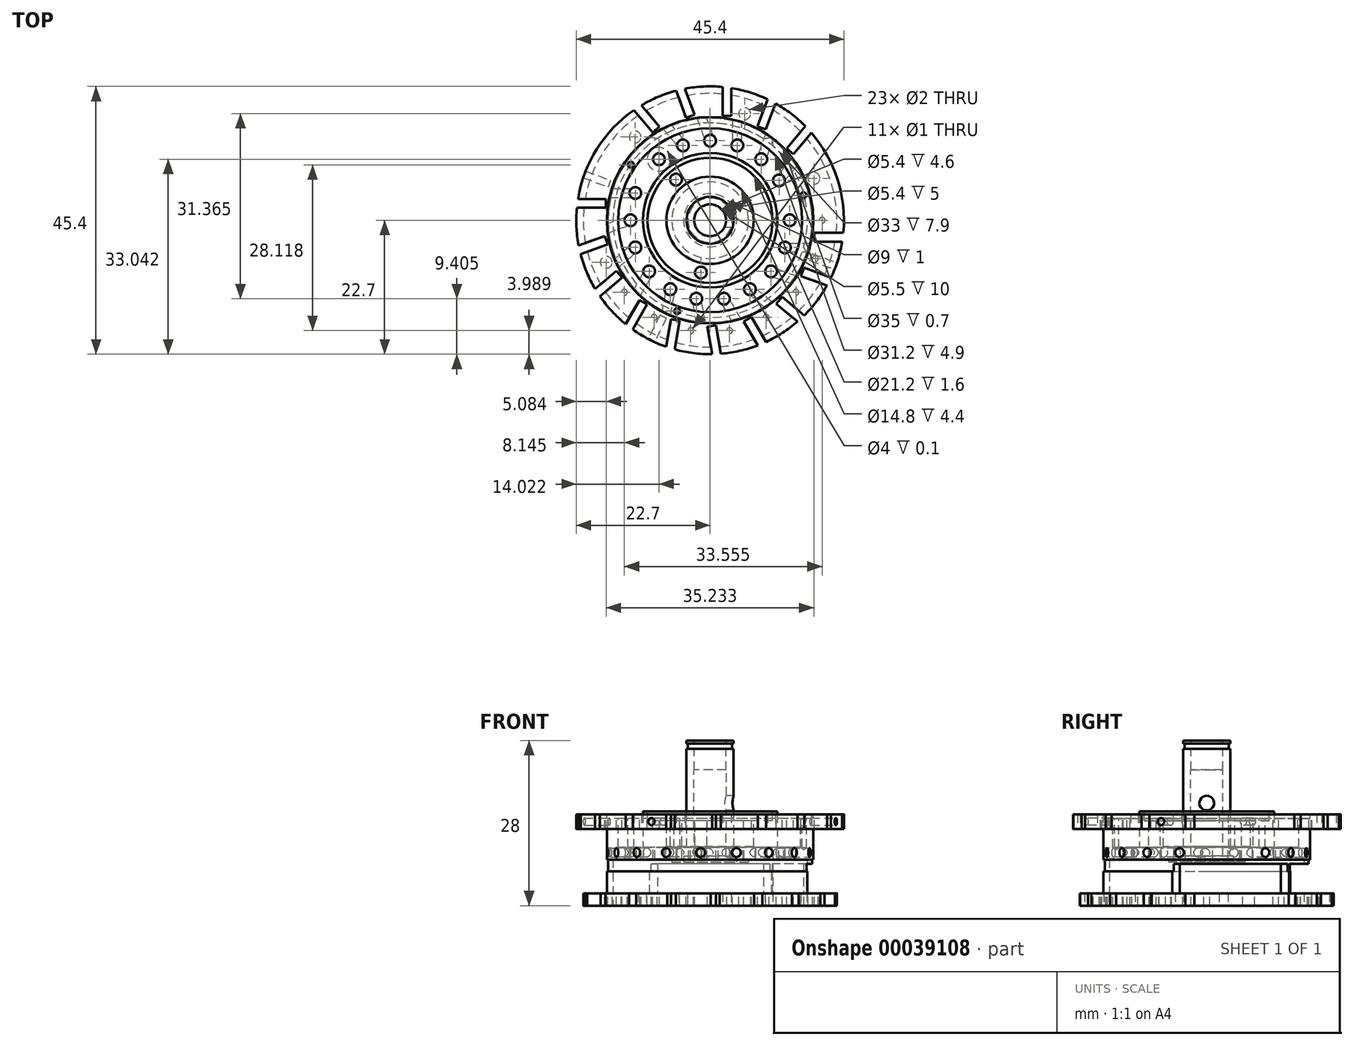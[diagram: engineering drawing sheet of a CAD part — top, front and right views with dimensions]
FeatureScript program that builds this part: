
annotation { "Feature Type Name" : "Feature", "Feature Type Description" : "" }
export const myFeature = defineFeature(function(context is Context, id is Id, definition is map)
    precondition{}
    {
        {
            var Q0;
            Q0=qCreatedBy(makeId("Front.planeOp"),FACE);
            var sketch = newSketch(context, id + "F0", { "sketchPlane" : qUnion([Q0])});
            skLineSegment(sketch, "E0", {"start": v(0, 12.5) * mm, "end": v(4, 12.5) * mm});
            skLineSegment(sketch, "E1", {"start": v(4, 12.5) * mm, "end": v(4, 12) * mm});
            skLineSegment(sketch, "E2", {"start": v(4, 12) * mm, "end": v(3.75, 12) * mm});
            skLineSegment(sketch, "E3", {"start": v(3.75, 12) * mm, "end": v(3.75, 11.1) * mm});
            skLineSegment(sketch, "E4", {"start": v(3.75, 11.1) * mm, "end": v(4, 11.1) * mm});
            skLineSegment(sketch, "E5", {"start": v(4, 11.1) * mm, "end": v(4, 0.5) * mm});
            skLineSegment(sketch, "E6", {"start": v(4, 0.5) * mm, "end": v(11.4, 0.5) * mm});
            skLineSegment(sketch, "E7", {"start": v(11.4, 0.5) * mm, "end": v(11.4, 0) * mm});
            skLineSegment(sketch, "E8", {"start": v(11.4, 0) * mm, "end": v(22.7, 0) * mm});
            skLineSegment(sketch, "E9", {"start": v(22.7, 0) * mm, "end": v(22.7, -2.5) * mm});
            skLineSegment(sketch, "E10", {"start": v(22.7, -2.5) * mm, "end": v(17.5, -2.5) * mm});
            skLineSegment(sketch, "E11", {"start": v(17.5, -2.5) * mm, "end": v(17.5, -7.7) * mm});
            skLineSegment(sketch, "E12", {"start": v(17.5, -7.7) * mm, "end": v(17.3, -7.7) * mm});
            skLineSegment(sketch, "E13", {"start": v(17.3, -7.7) * mm, "end": v(17.3, -9.7) * mm});
            skLineSegment(sketch, "E14", {"start": v(17.3, -9.7) * mm, "end": v(17.5, -9.7) * mm});
            skLineSegment(sketch, "E15", {"start": v(17.5, -9.7) * mm, "end": v(17.5, -13.4) * mm});
            skLineSegment(sketch, "E16", {"start": v(17.5, -13.4) * mm, "end": v(22.7, -13.4) * mm});
            skLineSegment(sketch, "E17", {"start": v(22.7, -13.4) * mm, "end": v(22.7, -15.5) * mm});
            skLineSegment(sketch, "E18", {"start": v(22.7, -15.5) * mm, "end": v(0, -15.5) * mm});
            skLineSegment(sketch, "E19", {"start": v(0, -15.5) * mm, "end": v(0, 12.5) * mm});
            skSolve(sketch);
        }
        {
            var Q0;
            Q0 = qSketchRegion(id + "F0", true);
            var Q1;
            Q1=sQuery(id+"F0.wireOp",EDGE,"E19");
            revolve(context, id + "F1", {"entities" : qUnion([Q0]), "axis" : qUnion([Q1]), "revolveType" : RevolveType.FULL});
        }
        {
            var Q0;
            Q0=qCreatedBy(makeId("Right.planeOp"),FACE);
            var sketch = newSketch(context, id + "F2", { "sketchPlane" : qUnion([Q0])});
            skCircle(sketch, "E20", {"center": v(0, 1.9) * mm, "radius": 1.25 * mm});
            skSolve(sketch);
        }
        {
            var Q0;
            Q0=makeQuery(id+"F2.imprint","IMPRINT",FACE,{"disambiguationData":[TD([[makeQuery(id+"F2.imprint","IMPRINT",EDGE,{"derivedFrom":sQuery(id+"F2.wireOp",EDGE,"E20")}),1.0]])]});
            extrude(context, id + "F3", {"entities" : qUnion([Q0]), "operationType" : NewBodyOperationType.REMOVE, "depth" : 5 * mm});
        }
        {
            var Q0;
            Q0=makeQuery(id+"F1.opRevolve","SWEPT_FACE",FACE,{"disambiguationData":[OSD([sQuery(id+"F0.wireOp",EDGE,"E0")])]});
            var sketch = newSketch(context, id + "F4", { "sketchPlane" : qUnion([Q0])});
            skCircle(sketch, "E21", {"center": v(0, 0) * mm, "radius": 2.7 * mm});
            skSolve(sketch);
        }
        {
            var Q0;
            Q0=makeQuery(id+"F4.imprint","IMPRINT",FACE,{"disambiguationData":[TD([[makeQuery(id+"F4.imprint","IMPRINT",EDGE,{"derivedFrom":sQuery(id+"F4.wireOp",EDGE,"E21")}),1.0]])]});
            var Q1;
            Q1=makeQuery(id+"F1.opRevolve","SWEPT_FACE",FACE,{"disambiguationData":[OSD([sQuery(id+"F0.wireOp",EDGE,"E18")])]});
            extrude(context, id + "F5", {"entities" : qUnion([Q0]), "operationType" : NewBodyOperationType.REMOVE, "endBound" : BoundingType.UP_TO_SURFACE, "oppositeDirection" : true, "endBoundEntityFace" : qUnion([Q1]), "depth" : 5 * mm});
        }
        {
            var Q0;
            Q0=makeQuery(id+"F1.opRevolve","SWEPT_FACE",FACE,{"disambiguationData":[OSD([sQuery(id+"F0.wireOp",EDGE,"E18")])]});
            var sketch = newSketch(context, id + "F6", { "sketchPlane" : qUnion([Q0])});
            skCircle(sketch, "E22", {"center": v(0, 0) * mm, "radius": 16.5 * mm});
            skSolve(sketch);
        }
        {
            var Q0;
            Q0=makeQuery(id+"F6.imprint","IMPRINT",FACE,{"disambiguationData":[TD([[makeQuery(id+"F6.imprint","IMPRINT",EDGE,{"derivedFrom":sQuery(id+"F6.wireOp",EDGE,"E22")}),1.0]])]});
            extrude(context, id + "F7", {"entities" : qUnion([Q0]), "operationType" : NewBodyOperationType.REMOVE, "oppositeDirection" : true, "depth" : 7.4 * mm});
        }
        {
            var Q0;
            Q0=makeQuery(id+"F7.boolean.opBoolean","COPY",FACE,{"derivedFrom":makeQuery(id+"F7.opExtrude","CAP_FACE",FACE,{"disambiguationData":[OSD([sQuery(id+"F6.wireOp",EDGE,"E22")])],"isStart":false})});
            var sketch = newSketch(context, id + "F8", { "sketchPlane" : qUnion([Q0])});
            skCircle(sketch, "E23", {"center": v(0, 0) * mm, "radius": 6.5 * mm});
            skCircle(sketch, "E24", {"center": v(0, 0) * mm, "radius": 16.5 * mm});
            skSolve(sketch);
        }
        {
            var Q0;
            Q0=makeQuery(id+"F8.imprint","IMPRINT",FACE,{"disambiguationData":[TD([[makeQuery(id+"F8.imprint","IMPRINT",EDGE,{"derivedFrom":sQuery(id+"F8.wireOp",EDGE,"E23")}),-1.0]])]});
            extrude(context, id + "F9", {"entities" : qUnion([Q0]), "operationType" : NewBodyOperationType.REMOVE, "oppositeDirection" : true, "depth" : 0.5 * mm});
        }
        {
            var Q0;
            Q0=makeQuery(id+"F7.boolean.opBoolean","COPY",FACE,{"derivedFrom":makeQuery(id+"F7.opExtrude","CAP_FACE",FACE,{"disambiguationData":[OSD([sQuery(id+"F6.wireOp",EDGE,"E22")])],"isStart":false})});
            var sketch = newSketch(context, id + "F10", { "sketchPlane" : qUnion([Q0])});
            skCircle(sketch, "E25", {"center": v(0, 0) * mm, "radius": 4.5 * mm});
            skSolve(sketch);
        }
        {
            var Q0;
            Q0=makeQuery(id+"F10.imprint","IMPRINT",FACE,{"disambiguationData":[TD([[makeQuery(id+"F10.imprint","IMPRINT",EDGE,{"derivedFrom":sQuery(id+"F10.wireOp",EDGE,"E25")}),1.0]])]});
            extrude(context, id + "F11", {"entities" : qUnion([Q0]), "operationType" : NewBodyOperationType.REMOVE, "oppositeDirection" : true, "depth" : 1 * mm});
        }
        {
            var Q0;
            Q0=qCreatedBy(makeId("Top.planeOp"),FACE);
            var sketch = newSketch(context, id + "F12", { "sketchPlane" : qUnion([Q0])});
            skCircle(sketch, "E26", {"center": v(0, 0) * mm, "radius": 2.75 * mm});
            skSolve(sketch);
        }
        {
            var Q0;
            Q0 = qSketchRegion(id + "F12", true);
            extrude(context, id + "F13", {"entities" : qUnion([Q0]), "operationType" : NewBodyOperationType.REMOVE, "oppositeDirection" : true, "depth" : 2.5 * mm, "hasSecondDirection" : true, "secondDirectionOppositeDirection" : false, "secondDirectionDepth" : 7.5 * mm});
        }
        {
            var Q0;
            Q0=makeQuery(id+"F1.opRevolve","SWEPT_FACE",FACE,{"disambiguationData":[OSD([sQuery(id+"F0.wireOp",EDGE,"E8")])]});
            var sketch = newSketch(context, id + "F14", { "sketchPlane" : qUnion([Q0])});
            skCircle(sketch, "E27", {"center": v(0, 0) * mm, "radius": 11.4 * mm});
            skCircle(sketch, "E28", {"center": v(0, 0) * mm, "radius": 15.6 * mm});
            skCircle(sketch, "E29", {"center": v(0, 0) * mm, "radius": 17.5 * mm});
            skSolve(sketch);
        }
        {
            var Q0;
            Q0=makeQuery(id+"F14.imprint","IMPRINT",FACE,{"disambiguationData":[TD([[makeQuery(id+"F14.imprint","IMPRINT",EDGE,{"derivedFrom":sQuery(id+"F14.wireOp",EDGE,"E27")}),1.0]])]});
            var Q1;
            Q1=makeQuery(id+"F14.imprint","IMPRINT",FACE,{"disambiguationData":[TD([[makeQuery(id+"F14.imprint","IMPRINT",EDGE,{"derivedFrom":sQuery(id+"F14.wireOp",EDGE,"E28")}),-1.0]])]});
            extrude(context, id + "F15", {"entities" : qUnion([Q0, Q1]), "operationType" : NewBodyOperationType.REMOVE, "oppositeDirection" : true, "depth" : 0.7 * mm});
        }
        {
            var Q0;
            Q0=makeQuery(id+"F14.imprint","IMPRINT",FACE,{"disambiguationData":[TD([[makeQuery(id+"F14.imprint","IMPRINT",EDGE,{"derivedFrom":sQuery(id+"F14.wireOp",EDGE,"E27")}),1.0]])]});
            extrude(context, id + "F16", {"entities" : qUnion([Q0]), "operationType" : NewBodyOperationType.REMOVE, "oppositeDirection" : true, "depth" : 5.6 * mm});
        }
        {
            var Q0;
            Q0=makeQuery(id+"F1.opRevolve","SWEPT_FACE",FACE,{"disambiguationData":[OSD([sQuery(id+"F0.wireOp",EDGE,"E6")])]});
            var sketch = newSketch(context, id + "F17", { "sketchPlane" : qUnion([Q0])});
            skCircle(sketch, "E30", {"center": v(0, 0) * mm, "radius": 7.4 * mm});
            skCircle(sketch, "E31", {"center": v(0, 0) * mm, "radius": 10.6 * mm});
            skSolve(sketch);
        }
        {
            var Q0;
            Q0=makeQuery(id+"F17.imprint","IMPRINT",FACE,{"disambiguationData":[TD([[makeQuery(id+"F17.imprint","IMPRINT",EDGE,{"derivedFrom":sQuery(id+"F17.wireOp",EDGE,"E30")}),1.0]])]});
            var Q1;
            Q1=makeQuery(id+"F17.imprint","IMPRINT",FACE,{"disambiguationData":[TD([[makeQuery(id+"F17.imprint","IMPRINT",EDGE,{"derivedFrom":sQuery(id+"F17.wireOp",EDGE,"E30")}),-1.0]])]});
            extrude(context, id + "F18", {"entities" : qUnion([Q0, Q1]), "operationType" : NewBodyOperationType.REMOVE, "oppositeDirection" : true, "depth" : 1.6 * mm});
        }
        {
            var Q0;
            Q0=makeQuery(id+"F17.imprint","IMPRINT",FACE,{"disambiguationData":[TD([[makeQuery(id+"F17.imprint","IMPRINT",EDGE,{"derivedFrom":sQuery(id+"F17.wireOp",EDGE,"E30")}),1.0]])]});
            extrude(context, id + "F19", {"entities" : qUnion([Q0]), "operationType" : NewBodyOperationType.REMOVE, "oppositeDirection" : true, "depth" : 6 * mm});
        }
        {
            var Q0;
            Q0=makeQuery(id+"F1.opRevolve","SWEPT_FACE",FACE,{"disambiguationData":[OSD([sQuery(id+"F0.wireOp",EDGE,"E16")])]});
            var sketch = newSketch(context, id + "F20", { "sketchPlane" : qUnion([Q0])});
            skLineSegment(sketch, "E32", {"start": v(0, 0) * mm, "end": v(60.85, 16.3) * mm, "construction": true});
            skPoint(sketch, "E33", {"position": v(60.34, 18.24) * mm});
            skLineSegment(sketch, "E34", {"start": v(60.85, 16.3) * mm, "end": v(60.34, 18.24) * mm, "construction": true});
            skCircle(sketch, "E35", {"center": v(60.34, 18.24) * mm, "radius": 50 * mm});
            skLineSegment(sketch, "E36", {"start": v(0, 0) * mm, "end": v(2.2, 62.96) * mm, "construction": true});
            skLineSegment(sketch, "E37", {"start": v(2.2, 62.96) * mm, "end": v(0.2, 63.03) * mm, "construction": true});
            skCircle(sketch, "E38", {"center": v(0.2, 63.03) * mm, "radius": 50 * mm});
            skSolve(sketch);
        }
        {
            var Q0;
            Q0 = qSketchRegion(id + "F20", true);
            extrude(context, id + "F21", {"entities" : qUnion([Q0]), "operationType" : NewBodyOperationType.REMOVE, "depth" : 5 * mm});
        }
        {
            var Q0;
            Q0=makeQuery(id+"F16.boolean.opBoolean","COPY",FACE,{"derivedFrom":makeQuery(id+"F16.opExtrude","CAP_FACE",FACE,{"disambiguationData":[OSD([sQuery(id+"F14.wireOp",EDGE,"E27"),sQuery(id+"F14.wireOp",EDGE,"E28")])],"isStart":false})});
            var sketch = newSketch(context, id + "F22", { "sketchPlane" : qUnion([Q0])});
            skCircle(sketch, "E39", {"center": v(13.5, 0) * mm, "radius": 1 * mm});
            skCircle(sketch, "E40", {"center": v(0, 0) * mm, "radius": 13.5 * mm, "construction": true});
            skCircle(sketch, "E41.1.0", {"center": v(12.69, -4.62) * mm, "radius": 1 * mm});
            skCircle(sketch, "E41.2.0", {"center": v(10.34, -8.68) * mm, "radius": 1 * mm});
            skCircle(sketch, "E41.3.0", {"center": v(6.75, -11.7) * mm, "radius": 1 * mm});
            skCircle(sketch, "E41.4.0", {"center": v(2.34, -13.3) * mm, "radius": 1 * mm});
            skCircle(sketch, "E41.5.0", {"center": v(-2.34, -13.3) * mm, "radius": 1 * mm});
            skCircle(sketch, "E41.6.0", {"center": v(-6.75, -11.7) * mm, "radius": 1 * mm});
            skCircle(sketch, "E41.7.0", {"center": v(-10.34, -8.68) * mm, "radius": 1 * mm});
            skCircle(sketch, "E41.8.0", {"center": v(-12.69, -4.62) * mm, "radius": 1 * mm});
            skCircle(sketch, "E41.9.0", {"center": v(-13.5, 0) * mm, "radius": 1 * mm});
            skCircle(sketch, "E41.10.0", {"center": v(-12.69, 4.62) * mm, "radius": 1 * mm});
            skLineSegment(sketch, "E41.anchor1", {"start": v(0, 0) * mm, "end": v(13.5, 0) * mm, "construction": true});
            skLineSegment(sketch, "E41.anchor2", {"start": v(0, 0) * mm, "end": v(-12.69, 4.62) * mm, "construction": true});
            skCircle(sketch, "E42", {"center": v(11.7, 6.75) * mm, "radius": 1 * mm});
            skLineSegment(sketch, "E43", {"start": v(11.7, 6.75) * mm, "end": v(0, 0) * mm, "construction": true});
            skCircle(sketch, "E44.1.0", {"center": v(8.68, 10.34) * mm, "radius": 1 * mm});
            skCircle(sketch, "E44.2.0", {"center": v(4.62, 12.69) * mm, "radius": 1 * mm});
            skCircle(sketch, "E44.3.0", {"center": v(0, 13.5) * mm, "radius": 1 * mm});
            skCircle(sketch, "E44.4.0", {"center": v(-4.62, 12.69) * mm, "radius": 1 * mm});
            skCircle(sketch, "E44.5.0", {"center": v(-8.68, 10.34) * mm, "radius": 1 * mm});
            skLineSegment(sketch, "E44.anchor1", {"start": v(0, 0) * mm, "end": v(11.7, 6.75) * mm, "construction": true});
            skLineSegment(sketch, "E44.anchor2", {"start": v(0, 0) * mm, "end": v(-8.68, 10.34) * mm, "construction": true});
            skSolve(sketch);
        }
        {
            var Q0;
            Q0=makeQuery(id+"F22.imprint","IMPRINT",FACE,{"disambiguationData":[TD([[makeQuery(id+"F22.imprint","IMPRINT",EDGE,{"derivedFrom":sQuery(id+"F22.wireOp",EDGE,"E39")}),1.0]])]});
            var Q1;
            Q1=makeQuery(id+"F22.imprint","IMPRINT",FACE,{"disambiguationData":[TD([[makeQuery(id+"F22.imprint","IMPRINT",EDGE,{"derivedFrom":sQuery(id+"F22.wireOp",EDGE,"E41.1.0")}),1.0]])]});
            var Q2;
            Q2=makeQuery(id+"F22.imprint","IMPRINT",FACE,{"disambiguationData":[TD([[makeQuery(id+"F22.imprint","IMPRINT",EDGE,{"derivedFrom":sQuery(id+"F22.wireOp",EDGE,"E41.2.0")}),1.0]])]});
            var Q3;
            Q3=makeQuery(id+"F22.imprint","IMPRINT",FACE,{"disambiguationData":[TD([[makeQuery(id+"F22.imprint","IMPRINT",EDGE,{"derivedFrom":sQuery(id+"F22.wireOp",EDGE,"E41.3.0")}),1.0]])]});
            var Q4;
            Q4=makeQuery(id+"F22.imprint","IMPRINT",FACE,{"disambiguationData":[TD([[makeQuery(id+"F22.imprint","IMPRINT",EDGE,{"derivedFrom":sQuery(id+"F22.wireOp",EDGE,"E41.4.0")}),1.0]])]});
            var Q5;
            Q5=makeQuery(id+"F22.imprint","IMPRINT",FACE,{"disambiguationData":[TD([[makeQuery(id+"F22.imprint","IMPRINT",EDGE,{"derivedFrom":sQuery(id+"F22.wireOp",EDGE,"E41.5.0")}),1.0]])]});
            var Q6;
            Q6=makeQuery(id+"F22.imprint","IMPRINT",FACE,{"disambiguationData":[TD([[makeQuery(id+"F22.imprint","IMPRINT",EDGE,{"derivedFrom":sQuery(id+"F22.wireOp",EDGE,"E41.6.0")}),1.0]])]});
            var Q7;
            Q7=makeQuery(id+"F22.imprint","IMPRINT",FACE,{"disambiguationData":[TD([[makeQuery(id+"F22.imprint","IMPRINT",EDGE,{"derivedFrom":sQuery(id+"F22.wireOp",EDGE,"E41.7.0")}),1.0]])]});
            var Q8;
            Q8=makeQuery(id+"F22.imprint","IMPRINT",FACE,{"disambiguationData":[TD([[makeQuery(id+"F22.imprint","IMPRINT",EDGE,{"derivedFrom":sQuery(id+"F22.wireOp",EDGE,"E41.8.0")}),1.0]])]});
            var Q9;
            Q9=makeQuery(id+"F22.imprint","IMPRINT",FACE,{"disambiguationData":[TD([[makeQuery(id+"F22.imprint","IMPRINT",EDGE,{"derivedFrom":sQuery(id+"F22.wireOp",EDGE,"E41.9.0")}),1.0]])]});
            var Q10;
            Q10=makeQuery(id+"F22.imprint","IMPRINT",FACE,{"disambiguationData":[TD([[makeQuery(id+"F22.imprint","IMPRINT",EDGE,{"derivedFrom":sQuery(id+"F22.wireOp",EDGE,"E41.10.0")}),1.0]])]});
            var Q11;
            Q11=makeQuery(id+"F22.imprint","IMPRINT",FACE,{"disambiguationData":[TD([[makeQuery(id+"F22.imprint","IMPRINT",EDGE,{"derivedFrom":sQuery(id+"F22.wireOp",EDGE,"E42")}),1.0]])]});
            var Q12;
            Q12=makeQuery(id+"F22.imprint","IMPRINT",FACE,{"disambiguationData":[TD([[makeQuery(id+"F22.imprint","IMPRINT",EDGE,{"derivedFrom":sQuery(id+"F22.wireOp",EDGE,"E44.1.0")}),1.0]])]});
            var Q13;
            Q13=makeQuery(id+"F22.imprint","IMPRINT",FACE,{"disambiguationData":[TD([[makeQuery(id+"F22.imprint","IMPRINT",EDGE,{"derivedFrom":sQuery(id+"F22.wireOp",EDGE,"E44.2.0")}),1.0]])]});
            var Q14;
            Q14=makeQuery(id+"F22.imprint","IMPRINT",FACE,{"disambiguationData":[TD([[makeQuery(id+"F22.imprint","IMPRINT",EDGE,{"derivedFrom":sQuery(id+"F22.wireOp",EDGE,"E44.3.0")}),1.0]])]});
            var Q15;
            Q15=makeQuery(id+"F22.imprint","IMPRINT",FACE,{"disambiguationData":[TD([[makeQuery(id+"F22.imprint","IMPRINT",EDGE,{"derivedFrom":sQuery(id+"F22.wireOp",EDGE,"E44.4.0")}),1.0]])]});
            var Q16;
            Q16=makeQuery(id+"F22.imprint","IMPRINT",FACE,{"disambiguationData":[TD([[makeQuery(id+"F22.imprint","IMPRINT",EDGE,{"derivedFrom":sQuery(id+"F22.wireOp",EDGE,"E44.5.0")}),1.0]])]});
            var Q17;
            Q17=makeQuery(id+"F9.boolean.opBoolean","COPY",FACE,{"derivedFrom":makeQuery(id+"F9.opExtrude","CAP_FACE",FACE,{"disambiguationData":[OSD([sQuery(id+"F8.wireOp",EDGE,"E23"),sQuery(id+"F8.wireOp",EDGE,"E24")])],"isStart":false})});
            extrude(context, id + "F23", {"entities" : qUnion([Q0, Q1, Q2, Q3, Q4, Q5, Q6, Q7, Q8, Q9, Q10, Q11, Q12, Q13, Q14, Q15, Q16]), "operationType" : NewBodyOperationType.REMOVE, "endBound" : BoundingType.UP_TO_SURFACE, "oppositeDirection" : true, "endBoundEntityFace" : qUnion([Q17]), "depth" : 25 * mm});
        }
        {
            var Q0;
            Q0=makeQuery(id+"F18.boolean.opBoolean","COPY",FACE,{"derivedFrom":makeQuery(id+"F18.opExtrude","CAP_FACE",FACE,{"disambiguationData":[OSD([sQuery(id+"F0.wireOp",EDGE,"E5"),sQuery(id+"F0.wireOp",EDGE,"E6"),sQuery(id+"F17.wireOp",EDGE,"E31")])],"isStart":false})});
            var sketch = newSketch(context, id + "F24", { "sketchPlane" : qUnion([Q0])});
            skCircle(sketch, "E45", {"center": v(0, 0) * mm, "radius": 9 * mm, "construction": true});
            skCircle(sketch, "E46", {"center": v(-5.79, 6.9) * mm, "radius": 1 * mm});
            skLineSegment(sketch, "E47", {"start": v(-5.79, 6.9) * mm, "end": v(0, 0) * mm, "construction": true});
            skCircle(sketch, "E48", {"center": v(-1.56, -8.86) * mm, "radius": 1 * mm});
            skLineSegment(sketch, "E49", {"start": v(0, 0) * mm, "end": v(-1.56, -8.86) * mm, "construction": true});
            skSolve(sketch);
        }
        {
            var Q0;
            Q0 = qSketchRegion(id + "F24", true);
            var Q1;
            Q1=makeQuery(id+"F9.boolean.opBoolean","COPY",FACE,{"derivedFrom":makeQuery(id+"F9.opExtrude","CAP_FACE",FACE,{"disambiguationData":[OSD([sQuery(id+"F8.wireOp",EDGE,"E23"),sQuery(id+"F8.wireOp",EDGE,"E24")])],"isStart":false})});
            extrude(context, id + "F25", {"entities" : qUnion([Q0]), "operationType" : NewBodyOperationType.REMOVE, "endBound" : BoundingType.UP_TO_SURFACE, "oppositeDirection" : true, "endBoundEntityFace" : qUnion([Q1]), "depth" : 25 * mm});
        }
        {
            var Q0;
            Q0=qCreatedBy(makeId("Top.planeOp"),FACE);
            cPlane(context, id + "F26", {"entities" : qUnion([Q0]), "cplaneType" : CPlaneType.OFFSET, "offset" : 6.5 * mm, "oppositeDirection" : true, "width" : 150 * mm, "height" : 150 * mm});
        }
        {
            var Q0;
            Q0=qCreatedBy(id+"F26.planeOp",FACE);
            var sketch = newSketch(context, id + "F27", { "sketchPlane" : qUnion([Q0])});
            skLineSegment(sketch, "E50", {"start": v(13.35, -3.87) * mm, "end": v(17.35, -3.87) * mm});
            skLineSegment(sketch, "E51", {"start": v(12.69, -4.62) * mm, "end": v(17.35, -4.62) * mm, "construction": true});
            skLineSegment(sketch, "E52", {"start": v(11.7, 6.75) * mm, "end": v(16.03, 9.25) * mm, "construction": true});
            skLineSegment(sketch, "E53", {"start": v(11.7, 6.75) * mm, "end": v(14.69, 10.32) * mm, "construction": true});
            skLineSegment(sketch, "E54", {"start": v(11.54, 7.74) * mm, "end": v(14.11, 10.8) * mm});
            skLineSegment(sketch, "E55", {"start": v(14.11, 10.8) * mm, "end": v(14.69, 10.32) * mm});
            skCircle(sketch, "E56.0", {"center": v(8.68, 10.34) * mm, "radius": 1 * mm, "construction": true});
            skLineSegment(sketch, "E57", {"start": v(8.68, 10.34) * mm, "end": v(11.89, 14.17) * mm, "construction": true});
            skLineSegment(sketch, "E58", {"start": v(8.68, 10.34) * mm, "end": v(10.28, 14.73) * mm, "construction": true});
            skLineSegment(sketch, "E59", {"start": v(13.35, -3.87) * mm, "end": v(13.35, -4.62) * mm});
            skLineSegment(sketch, "E60", {"start": v(13.35, -4.62) * mm, "end": v(17.35, -4.62) * mm, "construction": true});
            skLineSegment(sketch, "E61", {"start": v(17.35, -4.62) * mm, "end": v(17.35, -3.87) * mm});
            skLineSegment(sketch, "E62", {"start": v(13.35, -4.62) * mm, "end": v(17.35, -4.62) * mm});
            skLineSegment(sketch, "E63", {"start": v(11.54, 7.74) * mm, "end": v(12.12, 7.26) * mm});
            skLineSegment(sketch, "E64", {"start": v(12.12, 7.26) * mm, "end": v(14.69, 10.32) * mm});
            skPoint(sketch, "E65.orphan", {"position": v(15.26, 9.84) * mm});
            skLineSegment(sketch, "E66", {"start": v(8.83, 10.77) * mm, "end": v(10.2, 14.53) * mm});
            skLineSegment(sketch, "E67", {"start": v(10.2, 14.53) * mm, "end": v(9.5, 14.79) * mm});
            skLineSegment(sketch, "E68", {"start": v(9.5, 14.79) * mm, "end": v(8.13, 11.03) * mm});
            skLineSegment(sketch, "E69", {"start": v(8.13, 11.03) * mm, "end": v(8.83, 10.77) * mm});
            skCircle(sketch, "E70.0", {"center": v(4.62, 12.69) * mm, "radius": 1 * mm, "construction": true});
            skLineSegment(sketch, "E71", {"start": v(4.62, 12.69) * mm, "end": v(6.4, 17.58) * mm, "construction": true});
            skLineSegment(sketch, "E72", {"start": v(4.62, 12.69) * mm, "end": v(4.62, 17.19) * mm});
            skLineSegment(sketch, "E73", {"start": v(4.62, 17.19) * mm, "end": v(3.87, 17.19) * mm});
            skLineSegment(sketch, "E74", {"start": v(3.87, 17.19) * mm, "end": v(3.87, 12.69) * mm});
            skLineSegment(sketch, "E75", {"start": v(3.87, 12.69) * mm, "end": v(4.62, 12.69) * mm});
            skCircle(sketch, "E76.0", {"center": v(0, 13.5) * mm, "radius": 1 * mm, "construction": true});
            skLineSegment(sketch, "E77", {"start": v(0, 13.5) * mm, "end": v(0, 18.73) * mm, "construction": true});
            skLineSegment(sketch, "E78", {"start": v(0, 13.5) * mm, "end": v(-1.57, 17.82) * mm});
            skLineSegment(sketch, "E79", {"start": v(-1.57, 17.82) * mm, "end": v(-2.28, 17.57) * mm});
            skLineSegment(sketch, "E80", {"start": v(-2.28, 17.57) * mm, "end": v(-0.7, 13.24) * mm});
            skLineSegment(sketch, "E81", {"start": v(-0.7, 13.24) * mm, "end": v(0, 13.5) * mm});
            skCircle(sketch, "E82.0", {"center": v(-4.62, 12.69) * mm, "radius": 1 * mm, "construction": true});
            skLineSegment(sketch, "E83", {"start": v(-4.62, 12.69) * mm, "end": v(-6.86, 18.84) * mm, "construction": true});
            skLineSegment(sketch, "E84", {"start": v(-4.62, 12.69) * mm, "end": v(-7.57, 16.2) * mm});
            skLineSegment(sketch, "E85", {"start": v(-7.57, 16.2) * mm, "end": v(-8.15, 15.73) * mm});
            skLineSegment(sketch, "E86", {"start": v(-8.15, 15.73) * mm, "end": v(-5.2, 12.2) * mm});
            skLineSegment(sketch, "E87", {"start": v(-5.2, 12.2) * mm, "end": v(-4.62, 12.69) * mm});
            skCircle(sketch, "E88.0", {"center": v(-12.69, 4.62) * mm, "radius": 1 * mm, "construction": true});
            skLineSegment(sketch, "E89.bottom", {"start": v(-12.69, 4.62) * mm, "end": v(-17.29, 4.62) * mm});
            skLineSegment(sketch, "E89.top", {"start": v(-12.69, 3.87) * mm, "end": v(-17.29, 3.87) * mm});
            skLineSegment(sketch, "E89.left", {"start": v(-12.69, 4.62) * mm, "end": v(-12.69, 3.87) * mm});
            skLineSegment(sketch, "E89.right", {"start": v(-17.29, 4.62) * mm, "end": v(-17.29, 3.87) * mm});
            skCircle(sketch, "E90.0", {"center": v(-13.5, 0) * mm, "radius": 1 * mm, "construction": true});
            skLineSegment(sketch, "E91", {"start": v(-13.5, 0) * mm, "end": v(-17.82, -1.57) * mm});
            skLineSegment(sketch, "E92", {"start": v(-17.82, -1.57) * mm, "end": v(-17.57, -2.28) * mm});
            skLineSegment(sketch, "E93", {"start": v(-17.57, -2.28) * mm, "end": v(-13.24, -0.7) * mm});
            skLineSegment(sketch, "E94", {"start": v(-13.24, -0.7) * mm, "end": v(-13.5, 0) * mm});
            skCircle(sketch, "E95.0", {"center": v(-12.69, -4.62) * mm, "radius": 1 * mm, "construction": true});
            skLineSegment(sketch, "E96", {"start": v(-12.69, -4.62) * mm, "end": v(-19.66, -7.16) * mm, "construction": true});
            skLineSegment(sketch, "E97", {"start": v(-12.69, -4.62) * mm, "end": v(-16.2, -7.57) * mm});
            skLineSegment(sketch, "E98", {"start": v(-16.2, -7.57) * mm, "end": v(-15.73, -8.15) * mm});
            skLineSegment(sketch, "E99", {"start": v(-15.73, -8.15) * mm, "end": v(-12.2, -5.2) * mm});
            skLineSegment(sketch, "E100", {"start": v(-12.2, -5.2) * mm, "end": v(-12.69, -4.62) * mm});
            skCircle(sketch, "E101.0", {"center": v(-10.34, -8.68) * mm, "radius": 1 * mm, "construction": true});
            skLineSegment(sketch, "E102", {"start": v(-10.34, -8.68) * mm, "end": v(-15.57, -13.07) * mm, "construction": true});
            skLineSegment(sketch, "E103", {"start": v(-10.34, -8.68) * mm, "end": v(-12.84, -13) * mm});
            skLineSegment(sketch, "E104", {"start": v(-12.84, -13) * mm, "end": v(-12.2, -13.38) * mm});
            skLineSegment(sketch, "E105", {"start": v(-12.2, -13.38) * mm, "end": v(-9.7, -9.05) * mm});
            skLineSegment(sketch, "E106", {"start": v(-9.7, -9.05) * mm, "end": v(-10.34, -8.68) * mm});
            skCircle(sketch, "E107.0", {"center": v(-6.75, -11.7) * mm, "radius": 1 * mm, "construction": true});
            skLineSegment(sketch, "E108", {"start": v(-6.75, -11.7) * mm, "end": v(-9.35, -16.2) * mm, "construction": true});
            skLineSegment(sketch, "E109", {"start": v(-6.75, -11.7) * mm, "end": v(-7.62, -16.62) * mm});
            skLineSegment(sketch, "E110", {"start": v(-7.62, -16.62) * mm, "end": v(-6.88, -16.75) * mm});
            skLineSegment(sketch, "E111", {"start": v(-6.88, -16.75) * mm, "end": v(-6.01, -11.82) * mm});
            skLineSegment(sketch, "E112", {"start": v(-6.01, -11.82) * mm, "end": v(-6.75, -11.7) * mm});
            skCircle(sketch, "E113.0", {"center": v(-2.34, -13.3) * mm, "radius": 1 * mm, "construction": true});
            skLineSegment(sketch, "E114", {"start": v(-2.34, -13.3) * mm, "end": v(-3.24, -18.4) * mm, "construction": true});
            skLineSegment(sketch, "E115", {"start": v(-2.34, -13.3) * mm, "end": v(-1.48, -18.22) * mm});
            skLineSegment(sketch, "E116", {"start": v(-1.48, -18.22) * mm, "end": v(-0.74, -18.09) * mm});
            skLineSegment(sketch, "E117", {"start": v(-0.74, -18.09) * mm, "end": v(-1.6, -13.16) * mm});
            skLineSegment(sketch, "E118", {"start": v(-1.6, -13.16) * mm, "end": v(-2.34, -13.3) * mm});
            skCircle(sketch, "E119.0", {"center": v(2.34, -13.3) * mm, "radius": 1 * mm, "construction": true});
            skLineSegment(sketch, "E120", {"start": v(2.34, -13.3) * mm, "end": v(3.28, -18.57) * mm, "construction": true});
            skLineSegment(sketch, "E121", {"start": v(2.34, -13.3) * mm, "end": v(4.84, -17.63) * mm});
            skLineSegment(sketch, "E122", {"start": v(4.84, -17.63) * mm, "end": v(5.5, -17.25) * mm});
            skLineSegment(sketch, "E123", {"start": v(5.5, -17.25) * mm, "end": v(3, -12.92) * mm});
            skLineSegment(sketch, "E124", {"start": v(3, -12.92) * mm, "end": v(2.34, -13.3) * mm});
            skCircle(sketch, "E125.0", {"center": v(6.75, -11.7) * mm, "radius": 1 * mm, "construction": true});
            skLineSegment(sketch, "E126", {"start": v(6.75, -11.7) * mm, "end": v(9.36, -16.21) * mm, "construction": true});
            skLineSegment(sketch, "E127", {"start": v(6.75, -11.7) * mm, "end": v(10.58, -14.9) * mm});
            skLineSegment(sketch, "E128", {"start": v(10.58, -14.9) * mm, "end": v(11.06, -14.33) * mm});
            skLineSegment(sketch, "E129", {"start": v(11.06, -14.33) * mm, "end": v(7.23, -11.12) * mm});
            skLineSegment(sketch, "E130", {"start": v(7.23, -11.12) * mm, "end": v(6.75, -11.7) * mm});
            skCircle(sketch, "E131.0", {"center": v(10.34, -8.68) * mm, "radius": 1 * mm, "construction": true});
            skLineSegment(sketch, "E132", {"start": v(10.34, -8.68) * mm, "end": v(14.76, -12.38) * mm, "construction": true});
            skLineSegment(sketch, "E133", {"start": v(10.34, -8.68) * mm, "end": v(15.04, -10.39) * mm});
            skLineSegment(sketch, "E134", {"start": v(15.04, -10.39) * mm, "end": v(15.3, -9.68) * mm});
            skLineSegment(sketch, "E135", {"start": v(15.3, -9.68) * mm, "end": v(10.6, -7.97) * mm});
            skLineSegment(sketch, "E136", {"start": v(10.6, -7.97) * mm, "end": v(10.34, -8.68) * mm});
            skSolve(sketch);
        }
        {
            var Q0;
            Q0=makeQuery(id+"F27.imprint","IMPRINT",FACE,{"disambiguationData":[TD([[makeQuery(id+"F27.imprint","IMPRINT",EDGE,{"derivedFrom":sQuery(id+"F27.wireOp",EDGE,"E50")}),-1.0]])]});
            var Q1;
            Q1=sQuery(id+"F27.wireOp",EDGE,"E62");
            revolve(context, id + "F28", {"operationType" : NewBodyOperationType.REMOVE, "entities" : qUnion([Q0]), "axis" : qUnion([Q1]), "revolveType" : RevolveType.FULL, "oppositeDirection" : true});
        }
        {
            var Q0;
            Q0=makeQuery(id+"F27.imprint","IMPRINT",FACE,{"disambiguationData":[TD([[makeQuery(id+"F27.imprint","IMPRINT",EDGE,{"derivedFrom":sQuery(id+"F27.wireOp",EDGE,"E54")}),-1.0]])]});
            var Q1;
            Q1=sQuery(id+"F27.wireOp",EDGE,"E53");
            revolve(context, id + "F29", {"operationType" : NewBodyOperationType.REMOVE, "entities" : qUnion([Q0]), "axis" : qUnion([Q1]), "revolveType" : RevolveType.FULL});
        }
        {
            var Q0;
            Q0=makeQuery(id+"F27.imprint","IMPRINT",FACE,{"disambiguationData":[TD([[makeQuery(id+"F27.imprint","IMPRINT",EDGE,{"derivedFrom":sQuery(id+"F27.wireOp",EDGE,"E66")}),1.0]])]});
            var Q1;
            Q1=sQuery(id+"F27.wireOp",EDGE,"E66");
            revolve(context, id + "F30", {"operationType" : NewBodyOperationType.REMOVE, "entities" : qUnion([Q0]), "axis" : qUnion([Q1]), "revolveType" : RevolveType.FULL, "oppositeDirection" : true});
        }
        {
            var Q0;
            Q0=makeQuery(id+"F27.imprint","IMPRINT",FACE,{"disambiguationData":[TD([[makeQuery(id+"F27.imprint","IMPRINT",EDGE,{"derivedFrom":sQuery(id+"F27.wireOp",EDGE,"E72")}),1.0]])]});
            var Q1;
            Q1=sQuery(id+"F27.wireOp",EDGE,"E72");
            revolve(context, id + "F31", {"operationType" : NewBodyOperationType.REMOVE, "entities" : qUnion([Q0]), "axis" : qUnion([Q1]), "revolveType" : RevolveType.FULL, "oppositeDirection" : true});
        }
        {
            var Q0;
            Q0=makeQuery(id+"F27.imprint","IMPRINT",FACE,{"disambiguationData":[TD([[makeQuery(id+"F27.imprint","IMPRINT",EDGE,{"derivedFrom":sQuery(id+"F27.wireOp",EDGE,"E78")}),1.0]])]});
            var Q1;
            Q1=sQuery(id+"F27.wireOp",EDGE,"E78");
            revolve(context, id + "F32", {"operationType" : NewBodyOperationType.REMOVE, "entities" : qUnion([Q0]), "axis" : qUnion([Q1]), "revolveType" : RevolveType.FULL, "oppositeDirection" : true});
        }
        {
            var Q0;
            Q0=makeQuery(id+"F27.imprint","IMPRINT",FACE,{"disambiguationData":[TD([[makeQuery(id+"F27.imprint","IMPRINT",EDGE,{"derivedFrom":sQuery(id+"F27.wireOp",EDGE,"E78")}),1.0]])]});
            var Q1;
            Q1=sQuery(id+"F27.wireOp",EDGE,"E78");
            revolve(context, id + "F33", {"operationType" : NewBodyOperationType.REMOVE, "entities" : qUnion([Q0]), "axis" : qUnion([Q1]), "revolveType" : RevolveType.FULL, "oppositeDirection" : true});
        }
        {
            var Q0;
            Q0=makeQuery(id+"F27.imprint","IMPRINT",FACE,{"disambiguationData":[TD([[makeQuery(id+"F27.imprint","IMPRINT",EDGE,{"derivedFrom":sQuery(id+"F27.wireOp",EDGE,"E84")}),1.0]])]});
            var Q1;
            Q1=sQuery(id+"F27.wireOp",EDGE,"E84");
            revolve(context, id + "F34", {"operationType" : NewBodyOperationType.REMOVE, "entities" : qUnion([Q0]), "axis" : qUnion([Q1]), "revolveType" : RevolveType.FULL, "oppositeDirection" : true});
        }
        {
            var Q0;
            Q0=makeQuery(id+"F27.imprint","IMPRINT",FACE,{"disambiguationData":[TD([[makeQuery(id+"F27.imprint","IMPRINT",EDGE,{"derivedFrom":sQuery(id+"F27.wireOp",EDGE,"E89.bottom")}),1.0]])]});
            var Q1;
            Q1=sQuery(id+"F27.wireOp",EDGE,"E89.bottom");
            revolve(context, id + "F35", {"operationType" : NewBodyOperationType.REMOVE, "entities" : qUnion([Q0]), "axis" : qUnion([Q1]), "revolveType" : RevolveType.FULL});
        }
        {
            var Q0;
            Q0=makeQuery(id+"F27.imprint","IMPRINT",FACE,{"disambiguationData":[TD([[makeQuery(id+"F27.imprint","IMPRINT",EDGE,{"derivedFrom":sQuery(id+"F27.wireOp",EDGE,"E91")}),1.0]])]});
            var Q1;
            Q1=sQuery(id+"F27.wireOp",EDGE,"E91");
            revolve(context, id + "F36", {"operationType" : NewBodyOperationType.REMOVE, "entities" : qUnion([Q0]), "axis" : qUnion([Q1]), "revolveType" : RevolveType.FULL, "oppositeDirection" : true});
        }
        {
            var Q0;
            Q0=makeQuery(id+"F27.imprint","IMPRINT",FACE,{"disambiguationData":[TD([[makeQuery(id+"F27.imprint","IMPRINT",EDGE,{"derivedFrom":sQuery(id+"F27.wireOp",EDGE,"E97")}),1.0]])]});
            var Q1;
            Q1=sQuery(id+"F27.wireOp",EDGE,"E97");
            revolve(context, id + "F37", {"operationType" : NewBodyOperationType.REMOVE, "entities" : qUnion([Q0]), "axis" : qUnion([Q1]), "revolveType" : RevolveType.FULL, "oppositeDirection" : true});
        }
        {
            var Q0;
            Q0=makeQuery(id+"F27.imprint","IMPRINT",FACE,{"disambiguationData":[TD([[makeQuery(id+"F27.imprint","IMPRINT",EDGE,{"derivedFrom":sQuery(id+"F27.wireOp",EDGE,"E103")}),1.0]])]});
            var Q1;
            Q1=sQuery(id+"F27.wireOp",EDGE,"E103");
            revolve(context, id + "F38", {"operationType" : NewBodyOperationType.REMOVE, "entities" : qUnion([Q0]), "axis" : qUnion([Q1]), "revolveType" : RevolveType.FULL, "oppositeDirection" : true});
        }
        {
            var Q0;
            Q0=makeQuery(id+"F27.imprint","IMPRINT",FACE,{"disambiguationData":[TD([[makeQuery(id+"F27.imprint","IMPRINT",EDGE,{"derivedFrom":sQuery(id+"F27.wireOp",EDGE,"E109")}),1.0]])]});
            var Q1;
            Q1=sQuery(id+"F27.wireOp",EDGE,"E109");
            revolve(context, id + "F39", {"operationType" : NewBodyOperationType.REMOVE, "entities" : qUnion([Q0]), "axis" : qUnion([Q1]), "revolveType" : RevolveType.FULL, "oppositeDirection" : true});
        }
        {
            var Q0;
            Q0=makeQuery(id+"F27.imprint","IMPRINT",FACE,{"disambiguationData":[TD([[makeQuery(id+"F27.imprint","IMPRINT",EDGE,{"derivedFrom":sQuery(id+"F27.wireOp",EDGE,"E115")}),1.0]])]});
            var Q1;
            Q1=sQuery(id+"F27.wireOp",EDGE,"E115");
            revolve(context, id + "F40", {"operationType" : NewBodyOperationType.REMOVE, "entities" : qUnion([Q0]), "axis" : qUnion([Q1]), "revolveType" : RevolveType.FULL, "oppositeDirection" : true});
        }
        {
            var Q0;
            Q0=makeQuery(id+"F27.imprint","IMPRINT",FACE,{"disambiguationData":[TD([[makeQuery(id+"F27.imprint","IMPRINT",EDGE,{"derivedFrom":sQuery(id+"F27.wireOp",EDGE,"E121")}),1.0]])]});
            var Q1;
            Q1=sQuery(id+"F27.wireOp",EDGE,"E121");
            revolve(context, id + "F41", {"operationType" : NewBodyOperationType.REMOVE, "entities" : qUnion([Q0]), "axis" : qUnion([Q1]), "revolveType" : RevolveType.FULL, "oppositeDirection" : true});
        }
        {
            var Q0;
            Q0=makeQuery(id+"F27.imprint","IMPRINT",FACE,{"disambiguationData":[TD([[makeQuery(id+"F27.imprint","IMPRINT",EDGE,{"derivedFrom":sQuery(id+"F27.wireOp",EDGE,"E127")}),1.0]])]});
            var Q1;
            Q1=sQuery(id+"F27.wireOp",EDGE,"E127");
            revolve(context, id + "F42", {"operationType" : NewBodyOperationType.REMOVE, "entities" : qUnion([Q0]), "axis" : qUnion([Q1]), "revolveType" : RevolveType.FULL});
        }
        {
            var Q0;
            Q0=makeQuery(id+"F27.imprint","IMPRINT",FACE,{"disambiguationData":[TD([[makeQuery(id+"F27.imprint","IMPRINT",EDGE,{"derivedFrom":sQuery(id+"F27.wireOp",EDGE,"E133")}),1.0]])]});
            var Q1;
            Q1=sQuery(id+"F27.wireOp",EDGE,"E133");
            revolve(context, id + "F43", {"operationType" : NewBodyOperationType.REMOVE, "entities" : qUnion([Q0]), "axis" : qUnion([Q1]), "revolveType" : RevolveType.FULL, "oppositeDirection" : true});
        }
        {
            var Q0;
            Q0=makeQuery(id+"F1.opRevolve","SWEPT_FACE",FACE,{"disambiguationData":[OSD([sQuery(id+"F0.wireOp",EDGE,"E8")])]});
            var sketch = newSketch(context, id + "F44", { "sketchPlane" : qUnion([Q0])});
            skLineSegment(sketch, "E137.0", {"start": v(12.69, -4.62) * mm, "end": v(17.35, -4.62) * mm, "construction": true});
            skCircle(sketch, "E138.0", {"center": v(0, 0) * mm, "radius": 15.6 * mm, "construction": true});
            skPoint(sketch, "E139", {"position": v(14.9, -4.62) * mm});
            skLineSegment(sketch, "E140.bottom", {"start": v(17.7, -3.62) * mm, "end": v(23.5, -3.62) * mm});
            skLineSegment(sketch, "E140.top", {"start": v(17.7, -2.12) * mm, "end": v(23.5, -2.12) * mm});
            skLineSegment(sketch, "E140.left", {"start": v(17.7, -3.62) * mm, "end": v(17.7, -2.12) * mm});
            skLineSegment(sketch, "E140.right", {"start": v(23.5, -3.62) * mm, "end": v(23.5, -2.12) * mm});
            skLineSegment(sketch, "E141.0", {"start": v(11.7, 6.75) * mm, "end": v(14.69, 10.32) * mm, "construction": true});
            skLineSegment(sketch, "E142.0", {"start": v(8.68, 10.34) * mm, "end": v(10.28, 14.73) * mm, "construction": true});
            skLineSegment(sketch, "E143.0", {"start": v(4.62, 12.69) * mm, "end": v(4.62, 17.19) * mm, "construction": true});
            skLineSegment(sketch, "E144.0", {"start": v(0, 13.5) * mm, "end": v(-1.57, 17.82) * mm, "construction": true});
            skLineSegment(sketch, "E145.0", {"start": v(-4.62, 12.69) * mm, "end": v(-7.57, 16.2) * mm, "construction": true});
            skPoint(sketch, "E146", {"position": v(13.12, 8.45) * mm});
            skPoint(sketch, "E147", {"position": v(9.44, 12.42) * mm});
            skPoint(sketch, "E148", {"position": v(4.62, 14.9) * mm});
            skPoint(sketch, "E149", {"position": v(-0.76, 15.58) * mm});
            skPoint(sketch, "E150", {"position": v(-6.04, 14.38) * mm});
            skLineSegment(sketch, "E151", {"start": v(14.15, 11.23) * mm, "end": v(13, 12.2) * mm});
            skLineSegment(sketch, "E152", {"start": v(13, 12.2) * mm, "end": v(16.73, 16.64) * mm});
            skLineSegment(sketch, "E153", {"start": v(16.73, 16.64) * mm, "end": v(17.88, 15.68) * mm});
            skLineSegment(sketch, "E154", {"start": v(17.88, 15.68) * mm, "end": v(14.15, 11.23) * mm});
            skLineSegment(sketch, "E155", {"start": v(9.45, 15.4) * mm, "end": v(11.44, 20.85) * mm});
            skLineSegment(sketch, "E156", {"start": v(11.44, 20.85) * mm, "end": v(10.03, 21.36) * mm});
            skLineSegment(sketch, "E157", {"start": v(10.03, 21.36) * mm, "end": v(8.04, 15.9) * mm});
            skLineSegment(sketch, "E158", {"start": v(8.04, 15.9) * mm, "end": v(9.45, 15.4) * mm});
            skLineSegment(sketch, "E159", {"start": v(3.62, 17.7) * mm, "end": v(3.62, 23.5) * mm});
            skLineSegment(sketch, "E160", {"start": v(3.62, 23.5) * mm, "end": v(2.12, 23.5) * mm});
            skLineSegment(sketch, "E161", {"start": v(2.12, 23.5) * mm, "end": v(2.12, 17.7) * mm});
            skLineSegment(sketch, "E162", {"start": v(2.12, 17.7) * mm, "end": v(3.62, 17.7) * mm});
            skLineSegment(sketch, "E163", {"start": v(-2.65, 17.87) * mm, "end": v(-4.64, 23.32) * mm});
            skLineSegment(sketch, "E164", {"start": v(-4.64, 23.32) * mm, "end": v(-6.05, 22.8) * mm});
            skLineSegment(sketch, "E165", {"start": v(-6.05, 22.8) * mm, "end": v(-4.06, 17.36) * mm});
            skLineSegment(sketch, "E166", {"start": v(-4.06, 17.36) * mm, "end": v(-2.65, 17.87) * mm});
            skLineSegment(sketch, "E167", {"start": v(-8.6, 15.88) * mm, "end": v(-12.34, 20.33) * mm});
            skLineSegment(sketch, "E168", {"start": v(-12.34, 20.33) * mm, "end": v(-13.48, 19.36) * mm});
            skLineSegment(sketch, "E169", {"start": v(-13.48, 19.36) * mm, "end": v(-9.76, 14.92) * mm});
            skLineSegment(sketch, "E170", {"start": v(-9.76, 14.92) * mm, "end": v(-8.6, 15.88) * mm});
            skLineSegment(sketch, "E171.bottom", {"start": v(-17.7, 3.62) * mm, "end": v(-23.5, 3.62) * mm});
            skLineSegment(sketch, "E171.top", {"start": v(-17.7, 2.12) * mm, "end": v(-23.5, 2.12) * mm});
            skLineSegment(sketch, "E171.left", {"start": v(-17.7, 3.62) * mm, "end": v(-17.7, 2.12) * mm});
            skLineSegment(sketch, "E171.right", {"start": v(-23.5, 3.62) * mm, "end": v(-23.5, 2.12) * mm});
            skLineSegment(sketch, "E172.0", {"start": v(-12.69, 4.62) * mm, "end": v(-17.29, 4.62) * mm, "construction": true});
            skLineSegment(sketch, "E173.0", {"start": v(-13.5, 0) * mm, "end": v(-17.82, -1.57) * mm, "construction": true});
            skLineSegment(sketch, "E173.1", {"start": v(-12.69, -4.62) * mm, "end": v(-16.2, -7.57) * mm, "construction": true});
            skLineSegment(sketch, "E173.2", {"start": v(-10.34, -8.68) * mm, "end": v(-12.84, -13) * mm, "construction": true});
            skLineSegment(sketch, "E174.0", {"start": v(-6.75, -11.7) * mm, "end": v(-7.62, -16.62) * mm, "construction": true});
            skLineSegment(sketch, "E174.1", {"start": v(-2.34, -13.3) * mm, "end": v(-1.48, -18.22) * mm, "construction": true});
            skLineSegment(sketch, "E174.2", {"start": v(2.34, -13.3) * mm, "end": v(4.84, -17.63) * mm, "construction": true});
            skLineSegment(sketch, "E174.3", {"start": v(6.75, -11.7) * mm, "end": v(10.58, -14.9) * mm, "construction": true});
            skLineSegment(sketch, "E174.4", {"start": v(10.34, -8.68) * mm, "end": v(15.04, -10.39) * mm, "construction": true});
            skPoint(sketch, "E175", {"position": v(-14.9, 4.62) * mm});
            skPoint(sketch, "E176", {"position": v(-15.58, -0.76) * mm});
            skPoint(sketch, "E177", {"position": v(-14.38, -6.04) * mm});
            skPoint(sketch, "E178", {"position": v(-11.45, -10.6) * mm});
            skPoint(sketch, "E179", {"position": v(-7.13, -13.87) * mm});
            skPoint(sketch, "E180", {"position": v(-1.96, -15.48) * mm});
            skPoint(sketch, "E181", {"position": v(3.45, -15.21) * mm});
            skPoint(sketch, "E182", {"position": v(8.45, -13.12) * mm});
            skPoint(sketch, "E183", {"position": v(12.42, -9.44) * mm});
            skLineSegment(sketch, "E184", {"start": v(-17.87, -2.65) * mm, "end": v(-23.32, -4.64) * mm});
            skLineSegment(sketch, "E185", {"start": v(-23.32, -4.64) * mm, "end": v(-22.8, -6.05) * mm});
            skLineSegment(sketch, "E186", {"start": v(-22.8, -6.05) * mm, "end": v(-17.36, -4.06) * mm});
            skLineSegment(sketch, "E187", {"start": v(-17.36, -4.06) * mm, "end": v(-17.87, -2.65) * mm});
            skLineSegment(sketch, "E188", {"start": v(-15.88, -8.6) * mm, "end": v(-20.33, -12.34) * mm});
            skLineSegment(sketch, "E189", {"start": v(-20.33, -12.34) * mm, "end": v(-19.36, -13.48) * mm});
            skLineSegment(sketch, "E190", {"start": v(-19.36, -13.48) * mm, "end": v(-14.92, -9.76) * mm});
            skLineSegment(sketch, "E191", {"start": v(-14.92, -9.76) * mm, "end": v(-15.88, -8.6) * mm});
            skLineSegment(sketch, "E192", {"start": v(-11.98, -13.52) * mm, "end": v(-14.88, -18.54) * mm});
            skLineSegment(sketch, "E193", {"start": v(-14.88, -18.54) * mm, "end": v(-13.58, -19.3) * mm});
            skLineSegment(sketch, "E194", {"start": v(-13.58, -19.3) * mm, "end": v(-10.68, -14.27) * mm});
            skLineSegment(sketch, "E195", {"start": v(-10.68, -14.27) * mm, "end": v(-11.98, -13.52) * mm});
            skLineSegment(sketch, "E196", {"start": v(-6.64, -16.8) * mm, "end": v(-7.64, -22.52) * mm});
            skLineSegment(sketch, "E197", {"start": v(-7.64, -22.52) * mm, "end": v(-6.17, -22.78) * mm});
            skLineSegment(sketch, "E198", {"start": v(-6.17, -22.78) * mm, "end": v(-5.16, -17.06) * mm});
            skLineSegment(sketch, "E199", {"start": v(-5.16, -17.06) * mm, "end": v(-6.64, -16.8) * mm});
            skLineSegment(sketch, "E200", {"start": v(-0.49, -18.06) * mm, "end": v(0.52, -23.77) * mm});
            skLineSegment(sketch, "E201", {"start": v(0.52, -23.77) * mm, "end": v(2, -23.51) * mm});
            skLineSegment(sketch, "E202", {"start": v(2, -23.51) * mm, "end": v(0.99, -17.8) * mm});
            skLineSegment(sketch, "E203", {"start": v(0.99, -17.8) * mm, "end": v(-0.49, -18.06) * mm});
            skLineSegment(sketch, "E204", {"start": v(5.72, -17.14) * mm, "end": v(8.62, -22.16) * mm});
            skLineSegment(sketch, "E205", {"start": v(8.62, -22.16) * mm, "end": v(9.92, -21.41) * mm});
            skLineSegment(sketch, "E206", {"start": v(9.92, -21.41) * mm, "end": v(7.02, -16.39) * mm});
            skLineSegment(sketch, "E207", {"start": v(7.02, -16.39) * mm, "end": v(5.72, -17.14) * mm});
            skLineSegment(sketch, "E208", {"start": v(11.23, -14.15) * mm, "end": v(15.68, -17.88) * mm});
            skLineSegment(sketch, "E209", {"start": v(15.68, -17.88) * mm, "end": v(16.64, -16.73) * mm});
            skLineSegment(sketch, "E210", {"start": v(16.64, -16.73) * mm, "end": v(12.2, -13) * mm});
            skLineSegment(sketch, "E211", {"start": v(12.2, -13) * mm, "end": v(11.23, -14.15) * mm});
            skLineSegment(sketch, "E212", {"start": v(15.4, -9.45) * mm, "end": v(20.85, -11.44) * mm});
            skLineSegment(sketch, "E213", {"start": v(20.85, -11.44) * mm, "end": v(21.36, -10.03) * mm});
            skLineSegment(sketch, "E214", {"start": v(21.36, -10.03) * mm, "end": v(15.9, -8.04) * mm});
            skLineSegment(sketch, "E215", {"start": v(15.9, -8.04) * mm, "end": v(15.4, -9.45) * mm});
            skSolve(sketch);
        }
        {
            var Q0;
            Q0 = qSketchRegion(id + "F44", true);
            var Q1;
            Q1=makeQuery(id+"F1.opRevolve","SWEPT_FACE",FACE,{"disambiguationData":[OSD([sQuery(id+"F0.wireOp",EDGE,"E18")])]});
            extrude(context, id + "F45", {"entities" : qUnion([Q0]), "operationType" : NewBodyOperationType.REMOVE, "endBound" : BoundingType.UP_TO_SURFACE, "oppositeDirection" : true, "endBoundEntityFace" : qUnion([Q1]), "depth" : 25 * mm});
        }
        {
            var Q0;
            Q0=makeQuery(id+"F21.boolean.opBoolean","MERGE",FACE,{"derivedFrom":[makeQuery(id+"F1.opRevolve","SWEPT_FACE",FACE,{"disambiguationData":[OSD([sQuery(id+"F0.wireOp",EDGE,"E16")])]}),makeQuery(id+"F21.opExtrude","CAP_FACE",FACE,{"disambiguationData":[OSD([sQuery(id+"F20.wireOp",EDGE,"E35"),sQuery(id+"F20.wireOp",EDGE,"E38")])],"isStart":true})]});
            var sketch = newSketch(context, id + "F46", { "sketchPlane" : qUnion([Q0])});
            skCircle(sketch, "E216", {"center": v(17.62, 7.12) * mm, "radius": 1 * mm});
            skLineSegment(sketch, "E217", {"start": v(17.62, 7.12) * mm, "end": v(0, 0) * mm, "construction": true});
            skPoint(sketch, "E218.center", {"position": v(0, 0) * mm});
            skLineSegment(sketch, "E218.anchor1", {"start": v(0, 0) * mm, "end": v(17.62, 7.12) * mm, "construction": true});
            skCircle(sketch, "E219", {"center": v(5.87, 18.07) * mm, "radius": 1 * mm});
            skLineSegment(sketch, "E220", {"start": v(5.87, 18.07) * mm, "end": v(0, 0) * mm, "construction": true});
            skCircle(sketch, "E221", {"center": v(-12.71, 14.12) * mm, "radius": 1 * mm});
            skLineSegment(sketch, "E222", {"start": v(-12.71, 14.12) * mm, "end": v(0, 0) * mm, "construction": true});
            skCircle(sketch, "E223", {"center": v(-17.62, -7.12) * mm, "radius": 1 * mm});
            skLineSegment(sketch, "E224", {"start": v(0, 0) * mm, "end": v(-17.62, -7.12) * mm, "construction": true});
            skCircle(sketch, "E225", {"center": v(19, 0) * mm, "radius": 0.5 * mm});
            skCircle(sketch, "E226.1.0", {"center": v(17.85, -6.5) * mm, "radius": 0.5 * mm});
            skCircle(sketch, "E226.2.0", {"center": v(14.55, -12.21) * mm, "radius": 0.5 * mm});
            skCircle(sketch, "E226.3.0", {"center": v(9.5, -16.45) * mm, "radius": 0.5 * mm});
            skCircle(sketch, "E226.4.0", {"center": v(3.3, -18.71) * mm, "radius": 0.5 * mm});
            skCircle(sketch, "E226.5.0", {"center": v(-3.3, -18.71) * mm, "radius": 0.5 * mm});
            skCircle(sketch, "E226.6.0", {"center": v(-9.5, -16.45) * mm, "radius": 0.5 * mm});
            skCircle(sketch, "E226.7.0", {"center": v(-14.55, -12.21) * mm, "radius": 0.5 * mm});
            skLineSegment(sketch, "E226.anchor1", {"start": v(0, 0) * mm, "end": v(19, 0) * mm, "construction": true});
            skLineSegment(sketch, "E226.anchor2", {"start": v(0, 0) * mm, "end": v(-14.55, -12.21) * mm, "construction": true});
            skSolve(sketch);
        }
        {
            var Q0;
            Q0 = qSketchRegion(id + "F46", true);
            var Q1;
            Q1=makeQuery(id+"F1.opRevolve","SWEPT_FACE",FACE,{"disambiguationData":[OSD([sQuery(id+"F0.wireOp",EDGE,"E18")])]});
            extrude(context, id + "F47", {"entities" : qUnion([Q0]), "operationType" : NewBodyOperationType.REMOVE, "endBound" : BoundingType.UP_TO_SURFACE, "oppositeDirection" : true, "endBoundEntityFace" : qUnion([Q1]), "depth" : 25 * mm});
        }
        {
            var Q0;
            Q0=makeQuery(id+"F9.boolean.opBoolean","COPY",FACE,{"derivedFrom":makeQuery(id+"F9.opExtrude","CAP_FACE",FACE,{"disambiguationData":[OSD([sQuery(id+"F8.wireOp",EDGE,"E23"),sQuery(id+"F8.wireOp",EDGE,"E24")])],"isStart":false})});
            var sketch = newSketch(context, id + "F48", { "sketchPlane" : qUnion([Q0])});
            skCircle(sketch, "E227", {"center": v(-8.68, -10.34) * mm, "radius": 2 * mm});
            skSolve(sketch);
        }
        {
            var Q0;
            Q0=makeQuery(id+"F48.imprint","IMPRINT",FACE,{"disambiguationData":[TD([[makeQuery(id+"F48.imprint","IMPRINT",EDGE,{"derivedFrom":sQuery(id+"F48.wireOp",EDGE,"E227")}),1.0]])]});
            extrude(context, id + "F49", {"entities" : qUnion([Q0]), "operationType" : NewBodyOperationType.REMOVE, "oppositeDirection" : true, "depth" : 0.1 * mm});
        }
        {
            var Q0;
            Q0=makeQuery(id+"F15.boolean.opBoolean","COPY",FACE,{"derivedFrom":makeQuery(id+"F15.opExtrude","CAP_FACE",FACE,{"disambiguationData":[OSD([sQuery(id+"F14.wireOp",EDGE,"E27"),sQuery(id+"F14.wireOp",EDGE,"E29")])],"isStart":false})});
            var sketch = newSketch(context, id + "F50", { "sketchPlane" : qUnion([Q0])});
            skPoint(sketch, "E228", {"position": v(-13.43, 9.4) * mm});
            skLineSegment(sketch, "E229", {"start": v(-13.43, 9.4) * mm, "end": v(0, 0) * mm, "construction": true});
            skPoint(sketch, "E230", {"position": v(-5.6, -15.41) * mm});
            skLineSegment(sketch, "E231", {"start": v(-5.6, -15.41) * mm, "end": v(0, 0) * mm, "construction": true});
            skPoint(sketch, "E232", {"position": v(15.84, 4.24) * mm});
            skLineSegment(sketch, "E233", {"start": v(15.84, 4.24) * mm, "end": v(0, 0) * mm, "construction": true});
            skSolve(sketch);
        }
        {
            var Q0;
            Q0=sQuery(id+"F50.wireOp",VERTEX,"E228");
            var Q1;
            Q1=makeQuery(id+"F1.opRevolve","SWEPT_BODY",BODY,{"disambiguationData":[OSD([sQuery(id+"F0.wireOp",EDGE,"E0"),sQuery(id+"F0.wireOp",EDGE,"E1"),sQuery(id+"F0.wireOp",EDGE,"E2"),sQuery(id+"F0.wireOp",EDGE,"E3"),sQuery(id+"F0.wireOp",EDGE,"E4"),sQuery(id+"F0.wireOp",EDGE,"E5"),sQuery(id+"F0.wireOp",EDGE,"E6"),sQuery(id+"F0.wireOp",EDGE,"E7"),sQuery(id+"F0.wireOp",EDGE,"E8"),sQuery(id+"F0.wireOp",EDGE,"E9"),sQuery(id+"F0.wireOp",EDGE,"E10"),sQuery(id+"F0.wireOp",EDGE,"E11"),sQuery(id+"F0.wireOp",EDGE,"E12"),sQuery(id+"F0.wireOp",EDGE,"E13"),sQuery(id+"F0.wireOp",EDGE,"E14"),sQuery(id+"F0.wireOp",EDGE,"E15"),sQuery(id+"F0.wireOp",EDGE,"E16"),sQuery(id+"F0.wireOp",EDGE,"E17"),sQuery(id+"F0.wireOp",EDGE,"E18"),sQuery(id+"F0.wireOp",EDGE,"E19")])]});
            hole(context, id + "F51", {"style" : HoleStyle.SIMPLE, "holeDiameter" : 1 * mm, "endStyle" : HoleEndStyle.BLIND, "holeDepth" : 5 * mm, "locations" : qUnion([Q0]), "scope" : qUnion([Q1])});
        }
        {
            var Q0;
            Q0=sQuery(id+"F50.wireOp",VERTEX,"E232");
            var Q1;
            Q1=makeQuery(id+"F1.opRevolve","SWEPT_BODY",BODY,{"disambiguationData":[OSD([sQuery(id+"F0.wireOp",EDGE,"E0"),sQuery(id+"F0.wireOp",EDGE,"E1"),sQuery(id+"F0.wireOp",EDGE,"E2"),sQuery(id+"F0.wireOp",EDGE,"E3"),sQuery(id+"F0.wireOp",EDGE,"E4"),sQuery(id+"F0.wireOp",EDGE,"E5"),sQuery(id+"F0.wireOp",EDGE,"E6"),sQuery(id+"F0.wireOp",EDGE,"E7"),sQuery(id+"F0.wireOp",EDGE,"E8"),sQuery(id+"F0.wireOp",EDGE,"E9"),sQuery(id+"F0.wireOp",EDGE,"E10"),sQuery(id+"F0.wireOp",EDGE,"E11"),sQuery(id+"F0.wireOp",EDGE,"E12"),sQuery(id+"F0.wireOp",EDGE,"E13"),sQuery(id+"F0.wireOp",EDGE,"E14"),sQuery(id+"F0.wireOp",EDGE,"E15"),sQuery(id+"F0.wireOp",EDGE,"E16"),sQuery(id+"F0.wireOp",EDGE,"E17"),sQuery(id+"F0.wireOp",EDGE,"E18"),sQuery(id+"F0.wireOp",EDGE,"E19")])]});
            hole(context, id + "F52", {"style" : HoleStyle.SIMPLE, "holeDiameter" : 1 * mm, "endStyle" : HoleEndStyle.BLIND, "holeDepth" : 5 * mm, "locations" : qUnion([Q0]), "scope" : qUnion([Q1])});
        }
        {
            var Q0;
            Q0=sQuery(id+"F50.wireOp",VERTEX,"E230");
            var Q1;
            Q1=makeQuery(id+"F1.opRevolve","SWEPT_BODY",BODY,{"disambiguationData":[OSD([sQuery(id+"F0.wireOp",EDGE,"E0"),sQuery(id+"F0.wireOp",EDGE,"E1"),sQuery(id+"F0.wireOp",EDGE,"E2"),sQuery(id+"F0.wireOp",EDGE,"E3"),sQuery(id+"F0.wireOp",EDGE,"E4"),sQuery(id+"F0.wireOp",EDGE,"E5"),sQuery(id+"F0.wireOp",EDGE,"E6"),sQuery(id+"F0.wireOp",EDGE,"E7"),sQuery(id+"F0.wireOp",EDGE,"E8"),sQuery(id+"F0.wireOp",EDGE,"E9"),sQuery(id+"F0.wireOp",EDGE,"E10"),sQuery(id+"F0.wireOp",EDGE,"E11"),sQuery(id+"F0.wireOp",EDGE,"E12"),sQuery(id+"F0.wireOp",EDGE,"E13"),sQuery(id+"F0.wireOp",EDGE,"E14"),sQuery(id+"F0.wireOp",EDGE,"E15"),sQuery(id+"F0.wireOp",EDGE,"E16"),sQuery(id+"F0.wireOp",EDGE,"E17"),sQuery(id+"F0.wireOp",EDGE,"E18"),sQuery(id+"F0.wireOp",EDGE,"E19")])]});
            hole(context, id + "F53", {"style" : HoleStyle.SIMPLE, "holeDiameter" : 1 * mm, "endStyle" : HoleEndStyle.BLIND, "holeDepth" : 5 * mm, "locations" : qUnion([Q0]), "scope" : qUnion([Q1])});
        }
        {
            var Q0;
            Q0=makeQuery(id+"F1.opRevolve","SWEPT_FACE",FACE,{"disambiguationData":[OSD([sQuery(id+"F0.wireOp",EDGE,"E18")])]});
            var sketch = newSketch(context, id + "F54", { "sketchPlane" : qUnion([Q0])});
            skCircle(sketch, "E234", {"center": v(0, 0) * mm, "radius": 21.5 * mm});
            skCircle(sketch, "E235", {"center": v(0, 0) * mm, "radius": 24.5 * mm});
            skSolve(sketch);
        }
        {
            var Q0;
            Q0 = qSketchRegion(id + "F54", true);
            extrude(context, id + "F55", {"entities" : qUnion([Q0]), "operationType" : NewBodyOperationType.REMOVE, "oppositeDirection" : true, "depth" : 2.1 * mm});
        }
        {
            var Q0;
            Q0=qCreatedBy(makeId("Top.planeOp"),FACE);
            cPlane(context, id + "F56", {"entities" : qUnion([Q0]), "cplaneType" : CPlaneType.OFFSET, "offset" : 1.25 * mm, "oppositeDirection" : true, "width" : 150 * mm, "height" : 150 * mm});
        }
        {
            var Q0;
            Q0=qCreatedBy(id+"F56.planeOp",FACE);
            var sketch = newSketch(context, id + "F57", { "sketchPlane" : qUnion([Q0])});
            skArc(sketch, "E236.0", {"start": v(-22.4, 3.62) * mm, "mid": v(-19.2, 12.12) * mm, "end": v(-12.9, 18.67) * mm, "construction": true});
            skPoint(sketch, "E237", {"position": v(-21.33, 7.76) * mm});
            skLineSegment(sketch, "E238", {"start": v(-21.33, 7.76) * mm, "end": v(0, 0) * mm, "construction": true});
            skArc(sketch, "E239.0", {"start": v(-7.45, -21.44) * mm, "mid": v(-10.4, -20.18) * mm, "end": v(-13.13, -18.51) * mm, "construction": true});
            skPoint(sketch, "E240", {"position": v(-9.95, -20.4) * mm});
            skLineSegment(sketch, "E241", {"start": v(0, 0) * mm, "end": v(-9.95, -20.4) * mm, "construction": true});
            skArc(sketch, "E242.0", {"start": v(22.4, -3.62) * mm, "mid": v(21.68, -6.74) * mm, "end": v(20.51, -9.72) * mm});
            skPoint(sketch, "E243", {"position": v(21.33, -7.76) * mm});
            skLineSegment(sketch, "E244", {"start": v(0, 0) * mm, "end": v(21.33, -7.76) * mm, "construction": true});
            skLineSegment(sketch, "E245", {"start": v(-21.33, 7.76) * mm, "end": v(-17.1, 6.22) * mm});
            skLineSegment(sketch, "E246", {"start": v(-17.1, 6.22) * mm, "end": v(-16.89, 6.79) * mm});
            skLineSegment(sketch, "E247", {"start": v(-16.89, 6.79) * mm, "end": v(-21.12, 8.32) * mm});
            skLineSegment(sketch, "E248", {"start": v(-21.12, 8.32) * mm, "end": v(-21.33, 7.76) * mm});
            skLineSegment(sketch, "E249", {"start": v(-9.95, -20.4) * mm, "end": v(-7.97, -16.35) * mm});
            skLineSegment(sketch, "E250", {"start": v(-7.97, -16.35) * mm, "end": v(-8.51, -16.09) * mm});
            skLineSegment(sketch, "E251", {"start": v(-8.51, -16.09) * mm, "end": v(-10.49, -20.13) * mm});
            skLineSegment(sketch, "E252", {"start": v(-10.49, -20.13) * mm, "end": v(-9.95, -20.4) * mm});
            skLineSegment(sketch, "E253", {"start": v(21.33, -7.76) * mm, "end": v(17.1, -6.22) * mm});
            skLineSegment(sketch, "E254", {"start": v(17.1, -6.22) * mm, "end": v(17.3, -5.66) * mm});
            skLineSegment(sketch, "E255", {"start": v(17.3, -5.66) * mm, "end": v(21.53, -7.2) * mm});
            skLineSegment(sketch, "E256", {"start": v(21.53, -7.2) * mm, "end": v(21.33, -7.76) * mm});
            skSolve(sketch);
        }
        {
            var Q0;
            Q0=makeQuery(id+"F57.imprint","IMPRINT",FACE,{"disambiguationData":[TD([[makeQuery(id+"F57.imprint","IMPRINT",EDGE,{"derivedFrom":sQuery(id+"F57.wireOp",EDGE,"E245")}),1.0]])]});
            var Q1;
            Q1=sQuery(id+"F57.wireOp",EDGE,"E238");
            revolve(context, id + "F58", {"operationType" : NewBodyOperationType.REMOVE, "entities" : qUnion([Q0]), "axis" : qUnion([Q1]), "revolveType" : RevolveType.FULL, "oppositeDirection" : true});
        }
        {
            var Q0;
            Q0=makeQuery(id+"F57.imprint","IMPRINT",FACE,{"disambiguationData":[TD([[makeQuery(id+"F57.imprint","IMPRINT",EDGE,{"derivedFrom":sQuery(id+"F57.wireOp",EDGE,"E249")}),1.0]])]});
            var Q1;
            Q1=sQuery(id+"F57.wireOp",EDGE,"E241");
            revolve(context, id + "F59", {"operationType" : NewBodyOperationType.REMOVE, "entities" : qUnion([Q0]), "axis" : qUnion([Q1]), "revolveType" : RevolveType.FULL, "oppositeDirection" : true});
        }
        {
            var Q0;
            Q0=makeQuery(id+"F57.imprint","IMPRINT",FACE,{"disambiguationData":[TD([[makeQuery(id+"F57.imprint","IMPRINT",EDGE,{"derivedFrom":sQuery(id+"F57.wireOp",EDGE,"E253")}),-1.0]])]});
            var Q1;
            Q1=sQuery(id+"F57.wireOp",EDGE,"E244");
            revolve(context, id + "F60", {"operationType" : NewBodyOperationType.REMOVE, "entities" : qUnion([Q0]), "axis" : qUnion([Q1]), "revolveType" : RevolveType.FULL, "oppositeDirection" : true});
        }
    });
